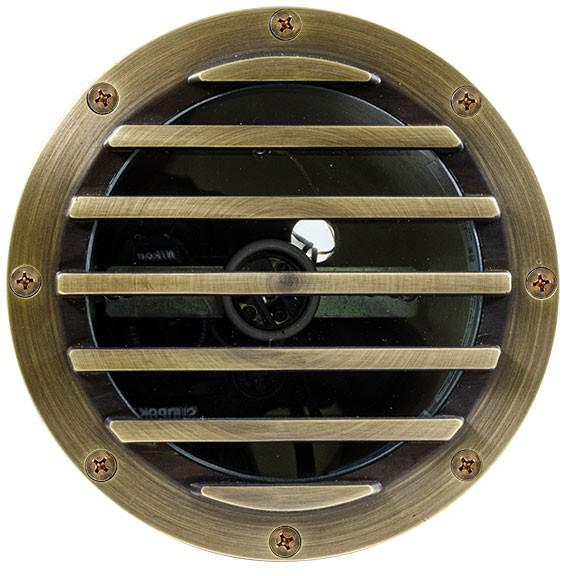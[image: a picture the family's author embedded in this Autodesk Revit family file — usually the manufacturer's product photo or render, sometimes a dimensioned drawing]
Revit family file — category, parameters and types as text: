
# Revit family: Alcon-9071-Revit-Family
name_source: partatom
category: Luminarias
units: mm (PartAtom-declared; Revit-internal decimal feet)

## family parameters
Anfitrión = Cara
Compartido = No
Corte con vacíos al cargar = No
Cota de conector redondo = Usar diámetro
Mantener orientación de anotación = No
Origen de luz = Sí
Punto de cálculo de habitación = No
Tipo de pieza = Normal

## types (1)
- Alcon-9071-Revit-Family
    Cambio de temperatura de color de luz atenuada = <Ninguno>
    Elevación por defecto = 4' - 0"
    Fabricante = Alcon Lighting
    Filtro de color = 16777215
    LENS GLASS = Glass
    Link to IES File = https://www.alconlighting.com
    Longitud de símbolo de origen de luz = 10' - 0"
    Modelo = Alcon Lighting 9071
    Product Data URL = https://www.alconlighting.com
    Product Page = https://www.alconlighting.com
    TOP FINISH = <Por categoría>
    URL = https://www.alconlighting.com
    Ángulo de campo de foco = 90.00°
    Ángulo de enfoque = 30.00°
    Ángulo de inclinación = 60.00°

## geometry (parser evidence)
native form markers: Sweep x3
no freeform markers — native parametric forms only
